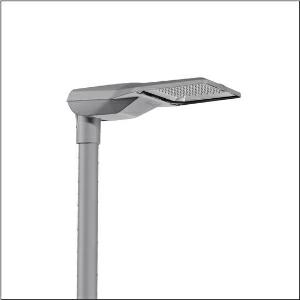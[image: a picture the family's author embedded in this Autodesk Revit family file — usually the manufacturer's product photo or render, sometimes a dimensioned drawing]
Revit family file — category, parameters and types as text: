
# Revit family: streetlight_sl_21_iq_midi___stw1_0a_5xe3e31d08mb_516a
name_source: partatom
category: Lighting Fixtures
units: mm (PartAtom-declared; Revit-internal decimal feet)

## family parameters
Cut with Voids When Loaded = No
Host = Face
Light Source = No
Part Type = Normal
Room Calculation Point = No
Round Connector Dimension = Use Diameter
Shared = No

## types (1)
- --- (1 x LED, 19500 lm, 146.7 W, 3000K)
    Apparent Load = 147 VA
    CIE Flux Codes = 38 75 98 100 100
    Color Rendering = 70
    Color Temperature = 3000K
    Default Elevation = 1800 mm
    Description = Streetlight SL 21 iQ midi, mast luminaire, primary light control with lens, of PMMA, primary optical cover: cover, of toughened safety glass, transparent, light distribution: STW1.0a, light emission: direct distribution, primary light characteristic: asymmetric, installation type: post-top, side-entry, LED, High Power LED, rated luminous flux: 19.500lm, luminous efficacy: 133lm/W, light colour: 730, colour temperature: 3000K, control: Auto-Match, Temp-Guard, Lumen-Switch, Night-Set, Smart-Wire, Light-Fading, Desk-Remote (wireless, voltage-free reading and setting of iQ features in the workshop via application-optimized NFC function/RFID function), optimised constant luminous flux control (CLO 2.0), pre-setting: linear dimming characteristic, mains connection: 230..240V, AC, 50/60Hz, start of lifetime: 147W, end of service life: 161W, reduction: 62W, luminaire housing, of diecast aluminium, powder-coated, Siteco® metallic grey (DB 702S), corrosivity category C5 mid according to DIN EN ISO 12944, please order mast flange separately, inclination adjustable: 0°, 5°, 10°, 15°, sealing non-destructively replaceable, multi-level sealing system, length: 644mm, width: 335mm, height: 110mm, mast flange for spigot size: 42mm (side-entry): 5XC10008XM4, 60/48mm (side-entry/post-top): 5XC10108XM2, 76/60mm (side-entry/post-top): 5XC10108XM1, protection rating (complete): IP66, insulation class (complete): insulation class II (safety insulation), certification: CE, ENEC, ENEC+, VDE, impact resistance: IK09, permissible operating ambient temperature for outdoor applications: -40..+50°C, standard-compliant lighting for roads and squares, packaging unit: 1 piece

Light Distribution: STW1.0a
    Height = 111 mm
    Lamp = 1 x LED
    Lamp Light Flux = 19500 lm
    Lamp Power = 146.7 W
    Lamp count = 1
    Length = 644 mm
    Luminous efficacy = 133 lm/W
    Manufacturer = Siteco
    ModVariant = No
    Model = 5XE3E31D08MB
    Number of Poles = 1
    OnlyDefault = Yes
    Power Factor = 1
    Product Name = Streetlight SL 21 iQ midi | STW1.0a
    Product group = mast luminaire | pylon top
    ProductGroupID = 6100
    Protection Class = Protection class II
    Protection Degree = IP 66
    RLX_Detail_Level = 1
    RLX_Emergency_Light_Flux = 0 lm
    RLX_Emergency_Type = 0
    RLX_Emergency_Type_DB = No
    RlxData = <blob elided: 91037 chars, md5=e6dfed91>
    Socket = socket
    Standby Power = 0 W
    System Light Flux = 19499 lm
    System Power = 147 W
    Type Comments = factory setting: luminous flux: 100 % | dim-lin: 254 | 753 mA
    Type Image = l_1004298.jpg
    URL = http://relux.com
    VarID = @adj_160251
    Voltage = 0 V
    Weight = 0.00 kg
    Width = 336 mm

## geometry (parser evidence)
native form markers: Blend x4, Sweep x9
no freeform markers — native parametric forms only
